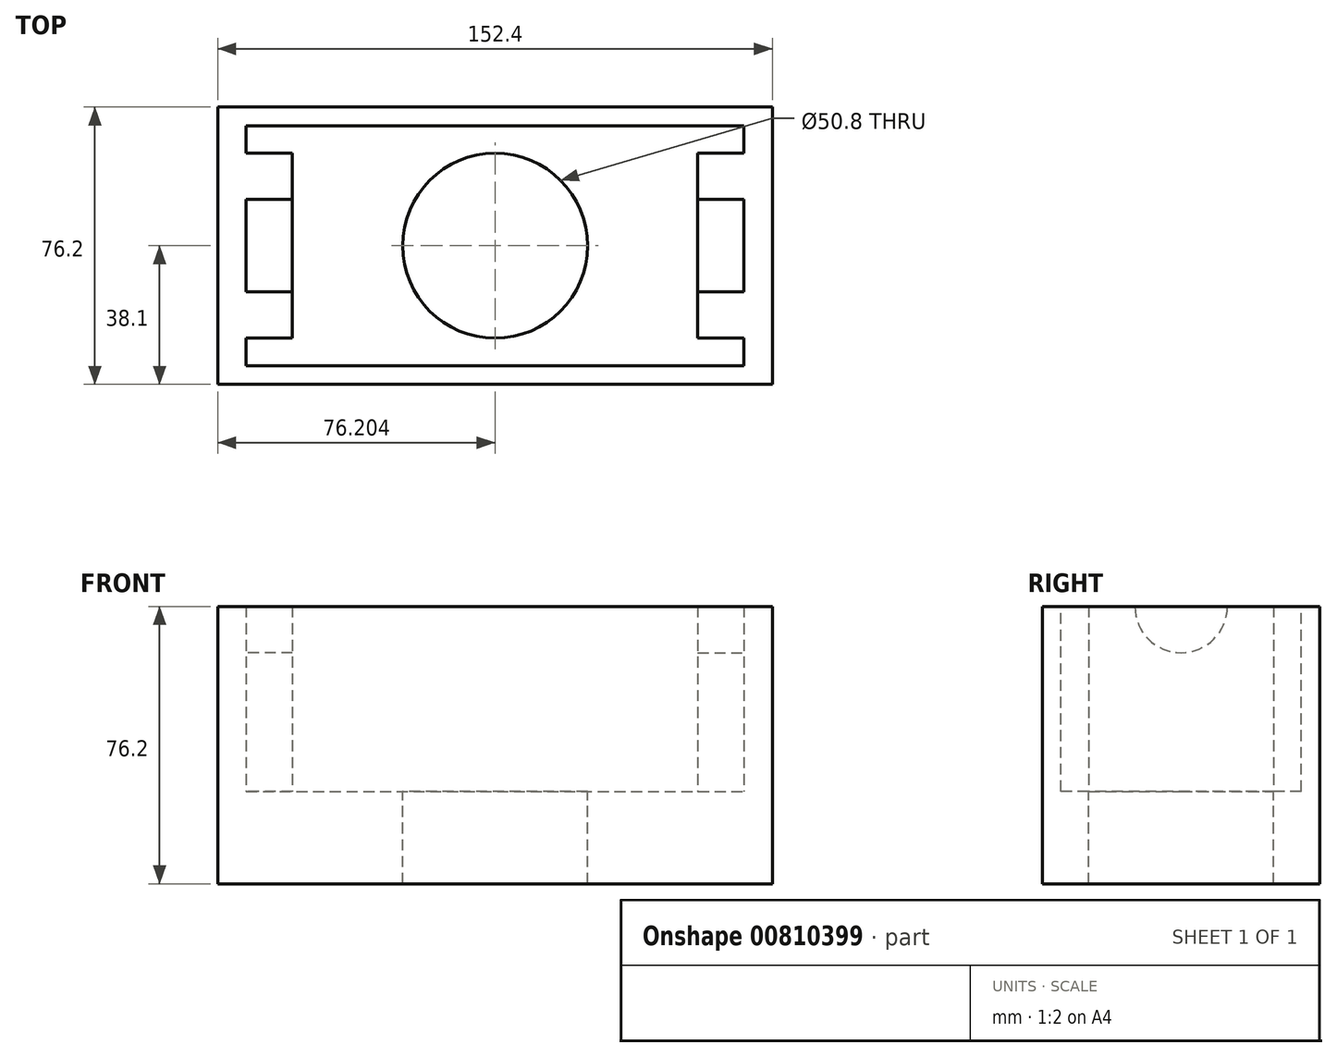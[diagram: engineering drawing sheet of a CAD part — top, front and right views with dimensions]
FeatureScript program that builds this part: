
annotation { "Feature Type Name" : "Feature", "Feature Type Description" : "" }
export const myFeature = defineFeature(function(context is Context, id is Id, definition is map)
    precondition{}
    {
        {
            var Q0;
            Q0=qCreatedBy(makeId("Front.planeOp"),FACE);
            var sketch = newSketch(context, id + "F0", { "sketchPlane" : qUnion([Q0])});
            skLineSegment(sketch, "E0.bottom", {"start": v(-92.95, 38.87) * mm, "end": v(59.45, 38.87) * mm});
            skLineSegment(sketch, "E0.top", {"start": v(-92.95, -37.33) * mm, "end": v(59.45, -37.33) * mm});
            skLineSegment(sketch, "E0.left", {"start": v(-92.95, 38.87) * mm, "end": v(-92.95, -37.33) * mm});
            skLineSegment(sketch, "E0.right", {"start": v(59.45, 38.87) * mm, "end": v(59.45, -37.33) * mm});
            skSolve(sketch);
        }
        {
            var Q0;
            Q0=makeQuery(id+"F0.imprint","IMPRINT",FACE,{"disambiguationData":[TD([[makeQuery(id+"F0.imprint","IMPRINT",EDGE,{"derivedFrom":sQuery(id+"F0.wireOp",EDGE,"E0.bottom")}),-1.0]])]});
            extrude(context, id + "F1", {"entities" : qUnion([Q0]), "depth" : 76.2 * mm, "offsetDistance" : 25.4 * mm});
        }
        {
            var Q0;
            Q0=makeQuery(id+"F1.opExtrude","SWEPT_FACE",FACE,{"disambiguationData":[OSD([sQuery(id+"F0.wireOp",EDGE,"E0.bottom")])]});
            var sketch = newSketch(context, id + "F2", { "sketchPlane" : qUnion([Q0])});
            skLineSegment(sketch, "E1.bottom", {"start": v(-85.14, -5.1) * mm, "end": v(51.64, -5.1) * mm});
            skLineSegment(sketch, "E1.top", {"start": v(-85.14, -71.1) * mm, "end": v(51.64, -71.1) * mm});
            skLineSegment(sketch, "E1.left", {"start": v(-85.14, -5.1) * mm, "end": v(-85.14, -71.1) * mm});
            skLineSegment(sketch, "E1.right", {"start": v(51.64, -5.1) * mm, "end": v(51.64, -71.1) * mm});
            skSolve(sketch);
        }
        {
            var Q0;
            Q0=makeQuery(id+"F2.imprint","IMPRINT",FACE,{"disambiguationData":[TD([[makeQuery(id+"F2.imprint","IMPRINT",EDGE,{"derivedFrom":sQuery(id+"F2.wireOp",EDGE,"E1.bottom")}),-1.0]])]});
            extrude(context, id + "F3", {"entities" : qUnion([Q0]), "operationType" : NewBodyOperationType.REMOVE, "oppositeDirection" : true, "depth" : 50.8 * mm, "offsetDistance" : 25.4 * mm});
        }
        {
            var Q0;
            Q0=makeQuery(id+"F3.boolean.opBoolean","COPY",FACE,{"derivedFrom":makeQuery(id+"F3.opExtrude","SWEPT_FACE",FACE,{"disambiguationData":[OSD([sQuery(id+"F2.wireOp",EDGE,"E1.left")])]})});
            var sketch = newSketch(context, id + "F4", { "sketchPlane" : qUnion([Q0])});
            skArc(sketch, "E2", {"start": v(-50.8, 38.87) * mm, "mid": v(-38.1, 26.17) * mm, "end": v(-25.4, 38.87) * mm});
            skLineSegment(sketch, "E3.bottom", {"start": v(-63.5, 38.87) * mm, "end": v(-50.8, 38.87) * mm});
            skLineSegment(sketch, "E3.top", {"start": v(-63.5, -11.93) * mm, "end": v(-12.7, -11.93) * mm});
            skLineSegment(sketch, "E3.left", {"start": v(-63.5, 38.87) * mm, "end": v(-63.5, -11.93) * mm});
            skLineSegment(sketch, "E3.right", {"start": v(-12.7, 38.87) * mm, "end": v(-12.7, -11.93) * mm});
            skLineSegment(sketch, "E4.trimOffspring", {"start": v(-25.4, 38.87) * mm, "end": v(-12.7, 38.87) * mm});
            skSolve(sketch);
        }
        {
            var Q0;
            Q0=makeQuery(id+"F4.imprint","IMPRINT",FACE,{"disambiguationData":[TD([[makeQuery(id+"F4.imprint","IMPRINT",EDGE,{"derivedFrom":sQuery(id+"F4.wireOp",EDGE,"E2")}),-1.0]])]});
            extrude(context, id + "F5", {"entities" : qUnion([Q0]), "operationType" : NewBodyOperationType.ADD, "depth" : 12.7 * mm, "offsetDistance" : 25.4 * mm});
        }
        {
            var Q0;
            Q0=makeQuery(id+"F3.boolean.opBoolean","COPY",FACE,{"derivedFrom":makeQuery(id+"F3.opExtrude","SWEPT_FACE",FACE,{"disambiguationData":[OSD([sQuery(id+"F2.wireOp",EDGE,"E1.right")])]})});
            var sketch = newSketch(context, id + "F6", { "sketchPlane" : qUnion([Q0])});
            skArc(sketch, "E5", {"start": v(25.4, 38.87) * mm, "mid": v(38.1, 26.17) * mm, "end": v(50.8, 38.87) * mm});
            skLineSegment(sketch, "E6.bottom", {"start": v(12.7, 38.87) * mm, "end": v(25.4, 38.87) * mm});
            skLineSegment(sketch, "E6.top", {"start": v(12.7, -11.93) * mm, "end": v(63.5, -11.93) * mm});
            skLineSegment(sketch, "E6.left", {"start": v(12.7, 38.87) * mm, "end": v(12.7, -11.93) * mm});
            skLineSegment(sketch, "E6.right", {"start": v(63.5, 38.87) * mm, "end": v(63.5, -11.93) * mm});
            skLineSegment(sketch, "E7.trimOffspring", {"start": v(50.8, 38.87) * mm, "end": v(63.5, 38.87) * mm});
            skSolve(sketch);
        }
        {
            var Q0;
            Q0=makeQuery(id+"F6.imprint","IMPRINT",FACE,{"disambiguationData":[TD([[makeQuery(id+"F6.imprint","IMPRINT",EDGE,{"derivedFrom":sQuery(id+"F6.wireOp",EDGE,"E5")}),-1.0]])]});
            extrude(context, id + "F7", {"entities" : qUnion([Q0]), "operationType" : NewBodyOperationType.ADD, "depth" : 12.7 * mm, "offsetDistance" : 25.4 * mm});
        }
        {
            var Q0;
            Q0=makeQuery(id+"F3.boolean.opBoolean","COPY",FACE,{"derivedFrom":makeQuery(id+"F3.opExtrude","CAP_FACE",FACE,{"disambiguationData":[OSD([sQuery(id+"F2.wireOp",EDGE,"E1.bottom"),sQuery(id+"F2.wireOp",EDGE,"E1.top"),sQuery(id+"F2.wireOp",EDGE,"E1.left"),sQuery(id+"F2.wireOp",EDGE,"E1.right")])],"isStart":false})});
            var sketch = newSketch(context, id + "F8", { "sketchPlane" : qUnion([Q0])});
            skCircle(sketch, "E8", {"center": v(-16.75, -38.1) * mm, "radius": 25.4 * mm});
            skPoint(sketch, "E8.centerSnap0", {"position": v(-16.75, -5.1) * mm});
            skPoint(sketch, "E9.start.orphan", {"position": v(-16.75, -71.1) * mm});
            skSolve(sketch);
        }
        {
            var Q0;
            Q0=makeQuery(id+"F8.imprint","IMPRINT",FACE,{"disambiguationData":[TD([[makeQuery(id+"F8.imprint","IMPRINT",EDGE,{"derivedFrom":sQuery(id+"F8.wireOp",EDGE,"E8")}),1.0]])]});
            extrude(context, id + "F9", {"entities" : qUnion([Q0]), "operationType" : NewBodyOperationType.REMOVE, "oppositeDirection" : true, "depth" : 66.04 * mm, "offsetDistance" : 25.4 * mm});
        }
    });
